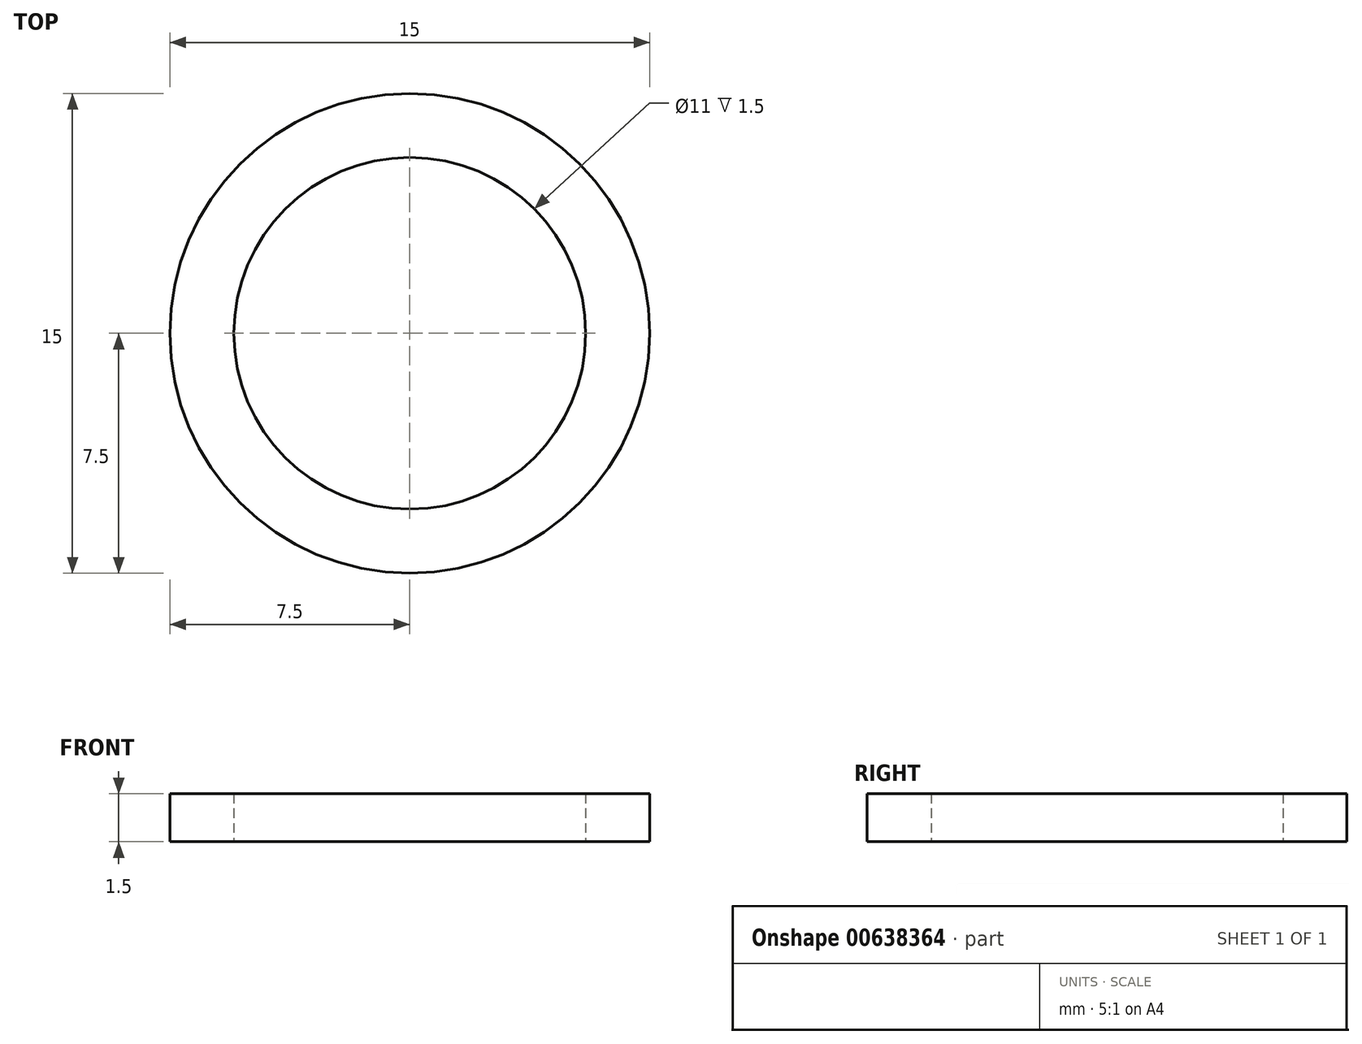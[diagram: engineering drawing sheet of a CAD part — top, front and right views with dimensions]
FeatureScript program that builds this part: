
annotation { "Feature Type Name" : "Feature", "Feature Type Description" : "" }
export const myFeature = defineFeature(function(context is Context, id is Id, definition is map)
    precondition{}
    {
        {
            var Q0;
            Q0=qCreatedBy(makeId("Top.planeOp"),FACE);
            var sketch = newSketch(context, id + "F0", { "sketchPlane" : qUnion([Q0])});
            skCircle(sketch, "E0", {"center": v(0, 0) * mm, "radius": 7.5 * mm});
            skCircle(sketch, "E1", {"center": v(0, 0) * mm, "radius": 5.5 * mm});
            skSolve(sketch);
        }
        {
            var Q0;
            Q0=makeQuery(id+"F0.imprint","IMPRINT",FACE,{"disambiguationData":[TD([[makeQuery(id+"F0.imprint","IMPRINT",EDGE,{"derivedFrom":sQuery(id+"F0.wireOp",EDGE,"E0")}),1.0]])]});
            extrude(context, id + "F1", {"entities" : qUnion([Q0]), "depth" : 1.5 * mm, "offsetDistance" : 25 * mm});
        }
    });
